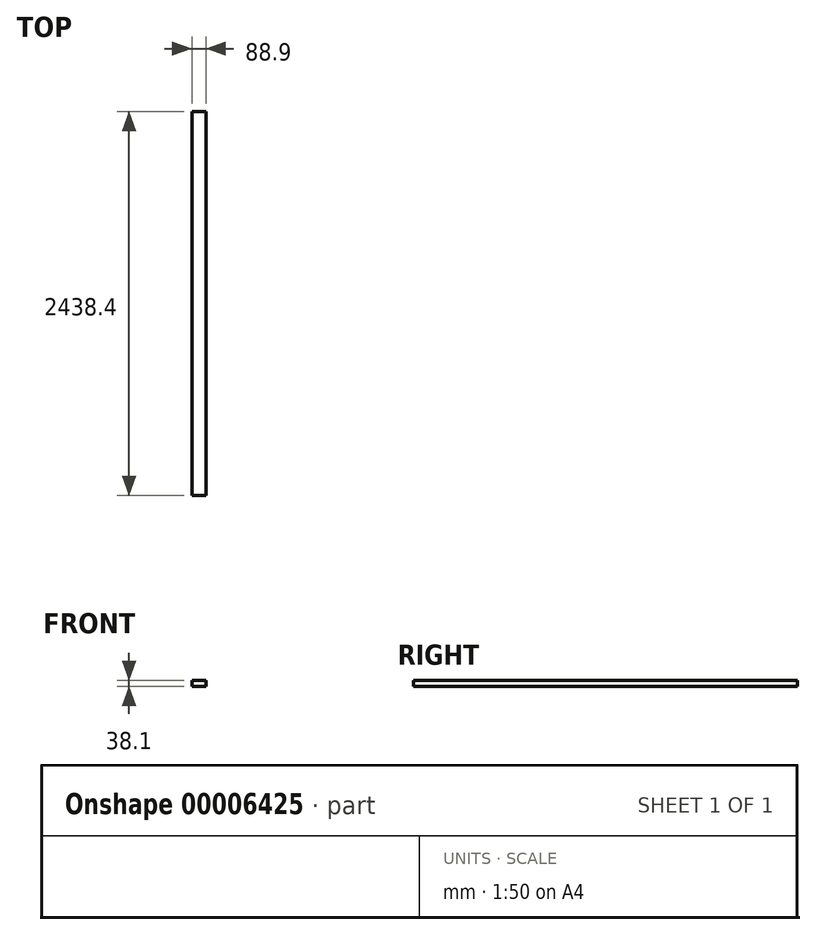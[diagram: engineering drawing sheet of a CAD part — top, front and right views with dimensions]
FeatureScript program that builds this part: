
annotation { "Feature Type Name" : "Feature", "Feature Type Description" : "" }
export const myFeature = defineFeature(function(context is Context, id is Id, definition is map)
    precondition{}
    {
        {
            var Q0;
            Q0=qCreatedBy(makeId("Front.planeOp"),FACE);
            var sketch = newSketch(context, id + "F0", { "sketchPlane" : qUnion([Q0])});
            skLineSegment(sketch, "E0.bottom", {"start": v(0, 0) * mm, "end": v(88.9, 0) * mm});
            skLineSegment(sketch, "E0.top", {"start": v(0, -38.1) * mm, "end": v(88.9, -38.1) * mm});
            skLineSegment(sketch, "E0.left", {"start": v(0, 0) * mm, "end": v(0, -38.1) * mm});
            skLineSegment(sketch, "E0.right", {"start": v(88.9, 0) * mm, "end": v(88.9, -38.1) * mm});
            skSolve(sketch);
        }
        {
            var Q0;
            Q0=makeQuery(id+"F0.imprint","IMPRINT",FACE,{"disambiguationData":[TD([[makeQuery(id+"F0.imprint","IMPRINT",EDGE,{"derivedFrom":sQuery(id+"F0.wireOp",EDGE,"E0.bottom")}),-1.0]])]});
            extrude(context, id + "F1", {"entities" : qUnion([Q0]), "depth" : 2438.4 * mm});
        }
    });
